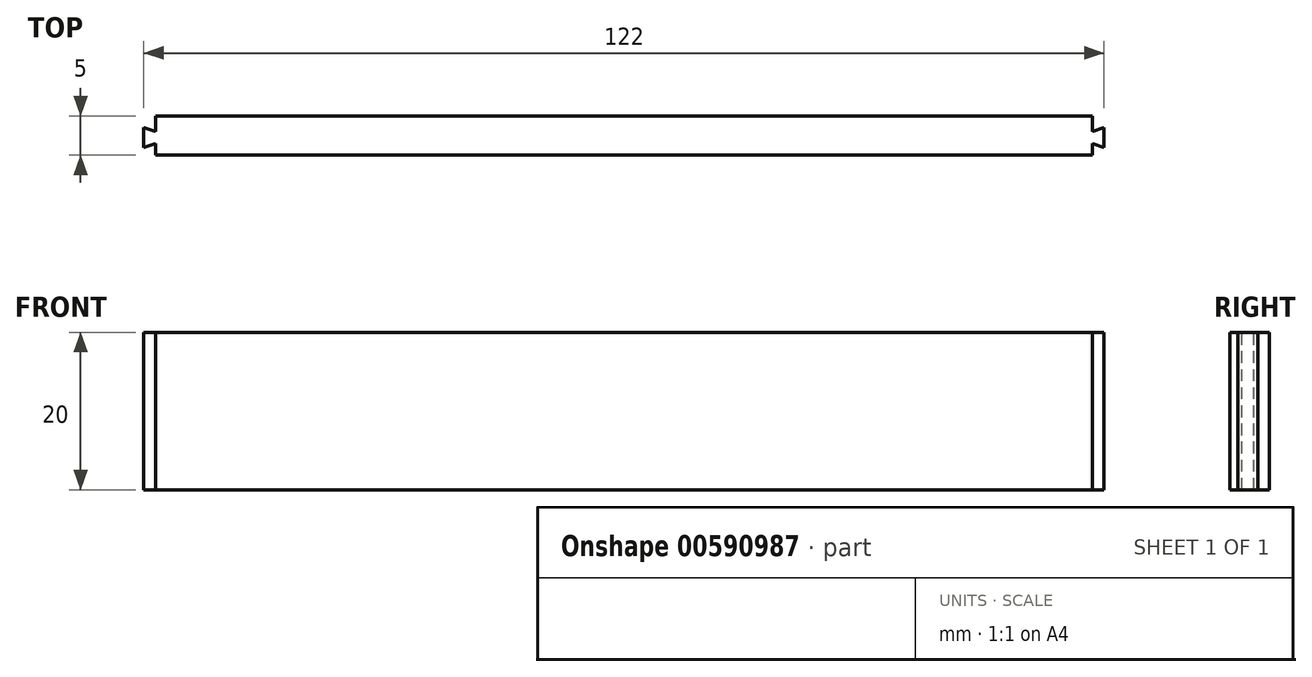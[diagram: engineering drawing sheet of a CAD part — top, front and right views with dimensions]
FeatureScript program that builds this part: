
annotation { "Feature Type Name" : "Feature", "Feature Type Description" : "" }
export const myFeature = defineFeature(function(context is Context, id is Id, definition is map)
    precondition{}
    {
        {
            var Q0;
            Q0=qCreatedBy(makeId("Front.planeOp"),FACE);
            var sketch = newSketch(context, id + "F0", { "sketchPlane" : qUnion([Q0])});
            skLineSegment(sketch, "E0.bottom", {"start": v(61, 10) * mm, "end": v(-61, 10) * mm});
            skLineSegment(sketch, "E0.top", {"start": v(61, -10) * mm, "end": v(-61, -10) * mm});
            skLineSegment(sketch, "E0.left", {"start": v(61, 10) * mm, "end": v(61, -10) * mm});
            skLineSegment(sketch, "E0.right", {"start": v(-61, 10) * mm, "end": v(-61, -10) * mm});
            skPoint(sketch, "E0.middle", {"position": v(0, 0) * mm});
            skSolve(sketch);
        }
        {
            var Q0;
            Q0=makeQuery(id+"F0.imprint","IMPRINT",FACE,{"disambiguationData":[TD([[makeQuery(id+"F0.imprint","IMPRINT",EDGE,{"derivedFrom":sQuery(id+"F0.wireOp",EDGE,"E0.bottom")}),1.0]])]});
            extrude(context, id + "F1", {"entities" : qUnion([Q0]), "depth" : 5 * mm, "offsetDistance" : 25 * mm});
        }
        {
            var Q0;
            Q0=makeQuery(id+"F1.opExtrude","SWEPT_FACE",FACE,{"disambiguationData":[OSD([sQuery(id+"F0.wireOp",EDGE,"E0.bottom")])]});
            var sketch = newSketch(context, id + "F2", { "sketchPlane" : qUnion([Q0])});
            skLineSegment(sketch, "E1", {"start": v(-59.5, 0) * mm, "end": v(-59.5, -2) * mm});
            skLineSegment(sketch, "E2", {"start": v(-59.5, -2) * mm, "end": v(-61, -1.5) * mm});
            skLineSegment(sketch, "E3", {"start": v(-61, -1.5) * mm, "end": v(-61, 0) * mm});
            skLineSegment(sketch, "E4", {"start": v(-61, 0) * mm, "end": v(-59.5, 0) * mm});
            skLineSegment(sketch, "E5", {"start": v(-61, -4) * mm, "end": v(-61, -5) * mm});
            skLineSegment(sketch, "E6", {"start": v(-61, -5) * mm, "end": v(-59.5, -5) * mm});
            skLineSegment(sketch, "E7", {"start": v(-59.5, -5) * mm, "end": v(-59.5, -3.5) * mm});
            skLineSegment(sketch, "E8", {"start": v(-59.5, -3.5) * mm, "end": v(-61, -4) * mm});
            skLineSegment(sketch, "E9", {"start": v(61, -5) * mm, "end": v(59.5, -5) * mm});
            skLineSegment(sketch, "E10", {"start": v(59.5, -5) * mm, "end": v(59.5, -3.5) * mm});
            skLineSegment(sketch, "E11", {"start": v(59.5, -3.5) * mm, "end": v(61, -4) * mm});
            skLineSegment(sketch, "E12", {"start": v(61, -4) * mm, "end": v(61, -5) * mm});
            skLineSegment(sketch, "E13", {"start": v(59.5, 0) * mm, "end": v(59.5, -2) * mm});
            skLineSegment(sketch, "E14", {"start": v(59.5, -2) * mm, "end": v(61, -1.5) * mm});
            skLineSegment(sketch, "E15", {"start": v(61, -1.5) * mm, "end": v(61, 0) * mm});
            skLineSegment(sketch, "E16", {"start": v(61, 0) * mm, "end": v(59.5, 0) * mm});
            skSolve(sketch);
        }
        {
            var Q0;
            Q0=makeQuery(id+"F2.imprint","IMPRINT",FACE,{"disambiguationData":[TD([[makeQuery(id+"F2.imprint","IMPRINT",EDGE,{"derivedFrom":sQuery(id+"F2.wireOp",EDGE,"E1")}),-1.0]])]});
            var Q1;
            Q1=makeQuery(id+"F2.imprint","IMPRINT",FACE,{"disambiguationData":[TD([[makeQuery(id+"F2.imprint","IMPRINT",EDGE,{"derivedFrom":sQuery(id+"F2.wireOp",EDGE,"E5")}),-1.0]])]});
            var Q2;
            Q2=makeQuery(id+"F2.imprint","IMPRINT",FACE,{"disambiguationData":[TD([[makeQuery(id+"F2.imprint","IMPRINT",EDGE,{"derivedFrom":sQuery(id+"F2.wireOp",EDGE,"E13")}),1.0]])]});
            var Q3;
            Q3=makeQuery(id+"F2.imprint","IMPRINT",FACE,{"disambiguationData":[TD([[makeQuery(id+"F2.imprint","IMPRINT",EDGE,{"derivedFrom":sQuery(id+"F2.wireOp",EDGE,"E9")}),-1.0]])]});
            extrude(context, id + "F3", {"entities" : qUnion([Q0, Q1, Q2, Q3]), "operationType" : NewBodyOperationType.REMOVE, "endBound" : BoundingType.THROUGH_ALL, "oppositeDirection" : true, "depth" : 25 * mm, "offsetDistance" : 25 * mm});
        }
    });
